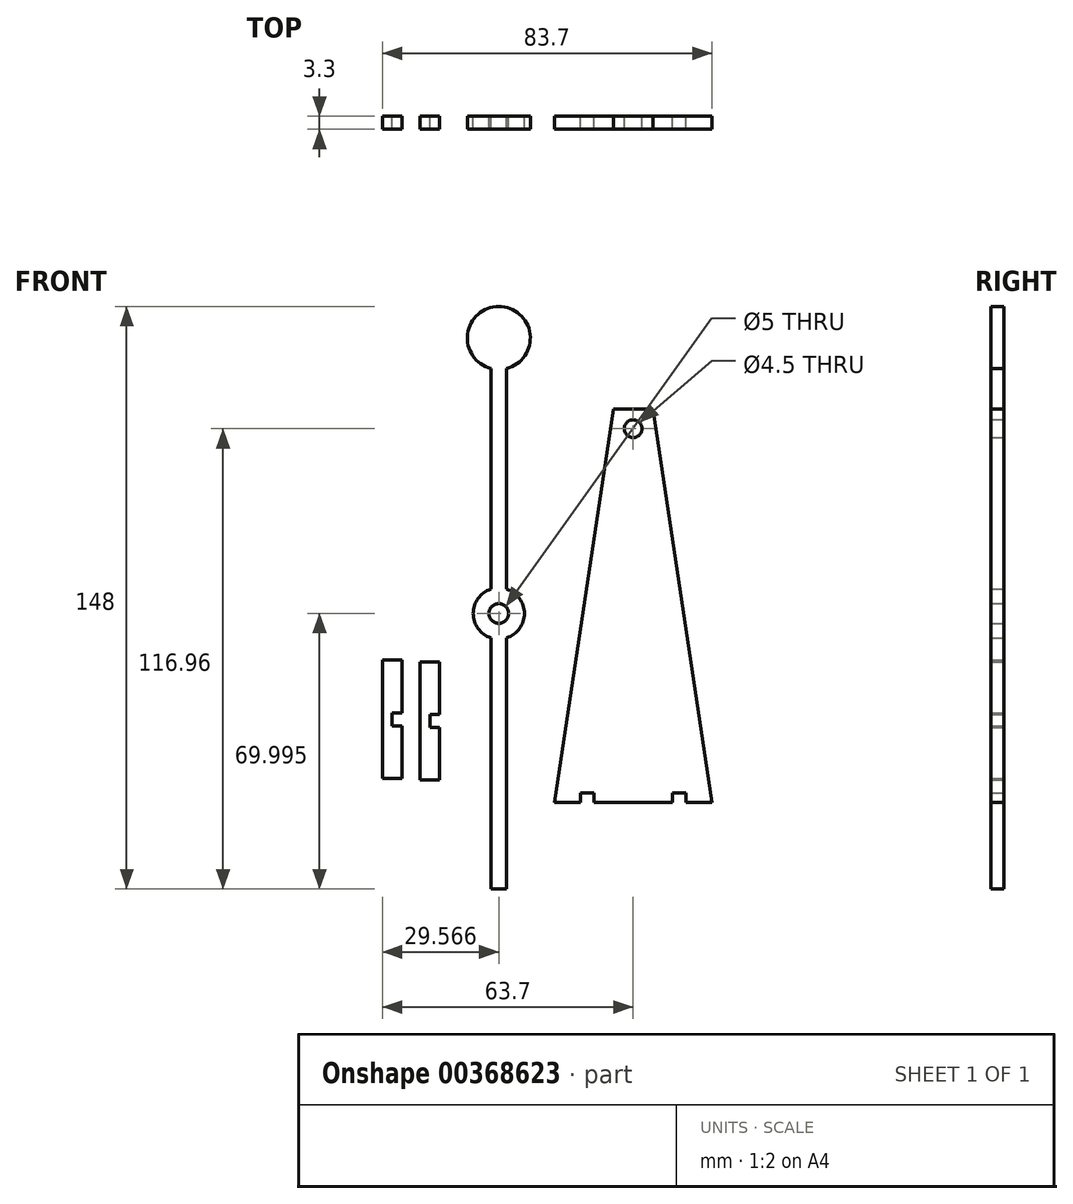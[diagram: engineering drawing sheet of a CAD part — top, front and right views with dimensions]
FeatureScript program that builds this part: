
annotation { "Feature Type Name" : "Feature", "Feature Type Description" : "" }
export const myFeature = defineFeature(function(context is Context, id is Id, definition is map)
    precondition{}
    {
        {
            var Q0;
            Q0=qCreatedBy(makeId("Front.planeOp"),FACE);
            var sketch = newSketch(context, id + "F0", { "sketchPlane" : qUnion([Q0])});
            skLineSegment(sketch, "E0", {"start": v(-20, 0) * mm, "end": v(-5, 100) * mm});
            skLineSegment(sketch, "E1", {"start": v(-5, 100) * mm, "end": v(5, 100) * mm});
            skLineSegment(sketch, "E2", {"start": v(5, 100) * mm, "end": v(20, 0) * mm});
            skLineSegment(sketch, "E3", {"start": v(-13.4, 0) * mm, "end": v(-13.4, 2.5) * mm});
            skLineSegment(sketch, "E4", {"start": v(-13.4, 2.5) * mm, "end": v(-10, 2.5) * mm});
            skLineSegment(sketch, "E5", {"start": v(-10, 2.5) * mm, "end": v(-10, 0) * mm});
            skLineSegment(sketch, "E6", {"start": v(10, 0) * mm, "end": v(10, 2.5) * mm});
            skLineSegment(sketch, "E7", {"start": v(10, 2.5) * mm, "end": v(13.4, 2.5) * mm});
            skLineSegment(sketch, "E8", {"start": v(13.4, 2.5) * mm, "end": v(13.4, 0) * mm});
            skLineSegment(sketch, "E9", {"start": v(-13.4, 0) * mm, "end": v(-20, 0) * mm});
            skLineSegment(sketch, "E10", {"start": v(-10, 0) * mm, "end": v(10, 0) * mm});
            skLineSegment(sketch, "E11", {"start": v(13.4, 0) * mm, "end": v(20, 0) * mm});
            skCircle(sketch, "E12", {"center": v(0, 95) * mm, "radius": 2.25 * mm});
            skSolve(sketch);
        }
        {
            var Q0;
            Q0=qCreatedBy(makeId("Front.planeOp"),FACE);
            var sketch = newSketch(context, id + "F1", { "sketchPlane" : qUnion([Q0])});
            skLineSegment(sketch, "E13", {"start": v(-63.7, 36.17) * mm, "end": v(-63.7, 6.17) * mm});
            skLineSegment(sketch, "E14", {"start": v(-63.7, 6.17) * mm, "end": v(-58.7, 6.17) * mm});
            skLineSegment(sketch, "E15", {"start": v(-58.7, 6.17) * mm, "end": v(-58.7, 19.52) * mm});
            skLineSegment(sketch, "E16", {"start": v(-58.7, 19.52) * mm, "end": v(-61.2, 19.52) * mm});
            skLineSegment(sketch, "E17", {"start": v(-61.2, 19.52) * mm, "end": v(-61.2, 22.82) * mm});
            skLineSegment(sketch, "E18", {"start": v(-61.2, 22.82) * mm, "end": v(-58.7, 22.82) * mm});
            skLineSegment(sketch, "E19", {"start": v(-58.7, 22.82) * mm, "end": v(-58.7, 36.17) * mm});
            skLineSegment(sketch, "E20", {"start": v(-58.7, 36.17) * mm, "end": v(-63.7, 36.17) * mm});
            skLineSegment(sketch, "E21", {"start": v(-54.16, 35.78) * mm, "end": v(-54.16, 5.78) * mm});
            skLineSegment(sketch, "E22", {"start": v(-54.16, 5.78) * mm, "end": v(-49.16, 5.78) * mm});
            skLineSegment(sketch, "E23", {"start": v(-49.16, 5.78) * mm, "end": v(-49.16, 19.13) * mm});
            skLineSegment(sketch, "E24", {"start": v(-49.16, 19.13) * mm, "end": v(-51.66, 19.13) * mm});
            skLineSegment(sketch, "E25", {"start": v(-51.66, 19.13) * mm, "end": v(-51.66, 22.43) * mm});
            skLineSegment(sketch, "E26", {"start": v(-51.66, 22.43) * mm, "end": v(-49.16, 22.43) * mm});
            skLineSegment(sketch, "E27", {"start": v(-49.16, 22.43) * mm, "end": v(-49.16, 35.78) * mm});
            skLineSegment(sketch, "E28", {"start": v(-49.16, 35.78) * mm, "end": v(-54.16, 35.78) * mm});
            skSolve(sketch);
        }
        {
            var Q0;
            Q0=makeQuery(id+"F0.imprint","IMPRINT",FACE,{"disambiguationData":[TD([[makeQuery(id+"F0.imprint","IMPRINT",EDGE,{"derivedFrom":sQuery(id+"F0.wireOp",EDGE,"E0")}),-1.0]])]});
            extrude(context, id + "F2", {"entities" : qUnion([Q0]), "depth" : 3.3 * mm});
        }
        {
            var Q0;
            Q0=makeQuery(id+"F1.imprint","IMPRINT",FACE,{"disambiguationData":[TD([[makeQuery(id+"F1.imprint","IMPRINT",EDGE,{"derivedFrom":sQuery(id+"F1.wireOp",EDGE,"E21")}),1.0]])]});
            var Q1;
            Q1=makeQuery(id+"F1.imprint","IMPRINT",FACE,{"disambiguationData":[TD([[makeQuery(id+"F1.imprint","IMPRINT",EDGE,{"derivedFrom":sQuery(id+"F1.wireOp",EDGE,"E13")}),1.0]])]});
            extrude(context, id + "F3", {"entities" : qUnion([Q0, Q1]), "depth" : 3.3 * mm});
        }
        {
            var Q0;
            Q0=qCreatedBy(makeId("Front.planeOp"),FACE);
            var sketch = newSketch(context, id + "F4", { "sketchPlane" : qUnion([Q0])});
            skLineSegment(sketch, "E29.top", {"start": v(-36.13, -21.96) * mm, "end": v(-32.13, -21.96) * mm});
            skLineSegment(sketch, "E29.left", {"start": v(-36.13, 110.29) * mm, "end": v(-36.13, 54.22) * mm});
            skLineSegment(sketch, "E29.right", {"start": v(-32.13, 110.29) * mm, "end": v(-32.13, 54.22) * mm});
            skCircle(sketch, "E30", {"center": v(-34.13, 48.04) * mm, "radius": 2.5 * mm});
            skArc(sketch, "E31", {"start": v(-36.13, 54.22) * mm, "mid": v(-40.63, 48.04) * mm, "end": v(-36.13, 41.85) * mm});
            skLineSegment(sketch, "E32.trimOffspring", {"start": v(-36.13, 41.85) * mm, "end": v(-36.13, -21.96) * mm});
            skLineSegment(sketch, "E33.trimOffspring", {"start": v(-32.13, 41.85) * mm, "end": v(-32.13, -21.96) * mm});
            skArc(sketch, "E34.trimOffspring", {"start": v(-32.13, 41.85) * mm, "mid": v(-27.63, 48.04) * mm, "end": v(-32.13, 54.22) * mm});
            skArc(sketch, "E35", {"start": v(-32.13, 110.29) * mm, "mid": v(-34.13, 126.04) * mm, "end": v(-36.13, 110.29) * mm});
            skPoint(sketch, "E36.orphan", {"position": v(-32.13, 118.04) * mm});
            skPoint(sketch, "E29.bottom.start.orphan", {"position": v(-36.13, 118.04) * mm});
            skSolve(sketch);
        }
        {
            var Q0;
            Q0 = qSketchRegion(id + "F4", true);
            extrude(context, id + "F5", {"entities" : qUnion([Q0]), "depth" : 3.3 * mm});
        }
    });
